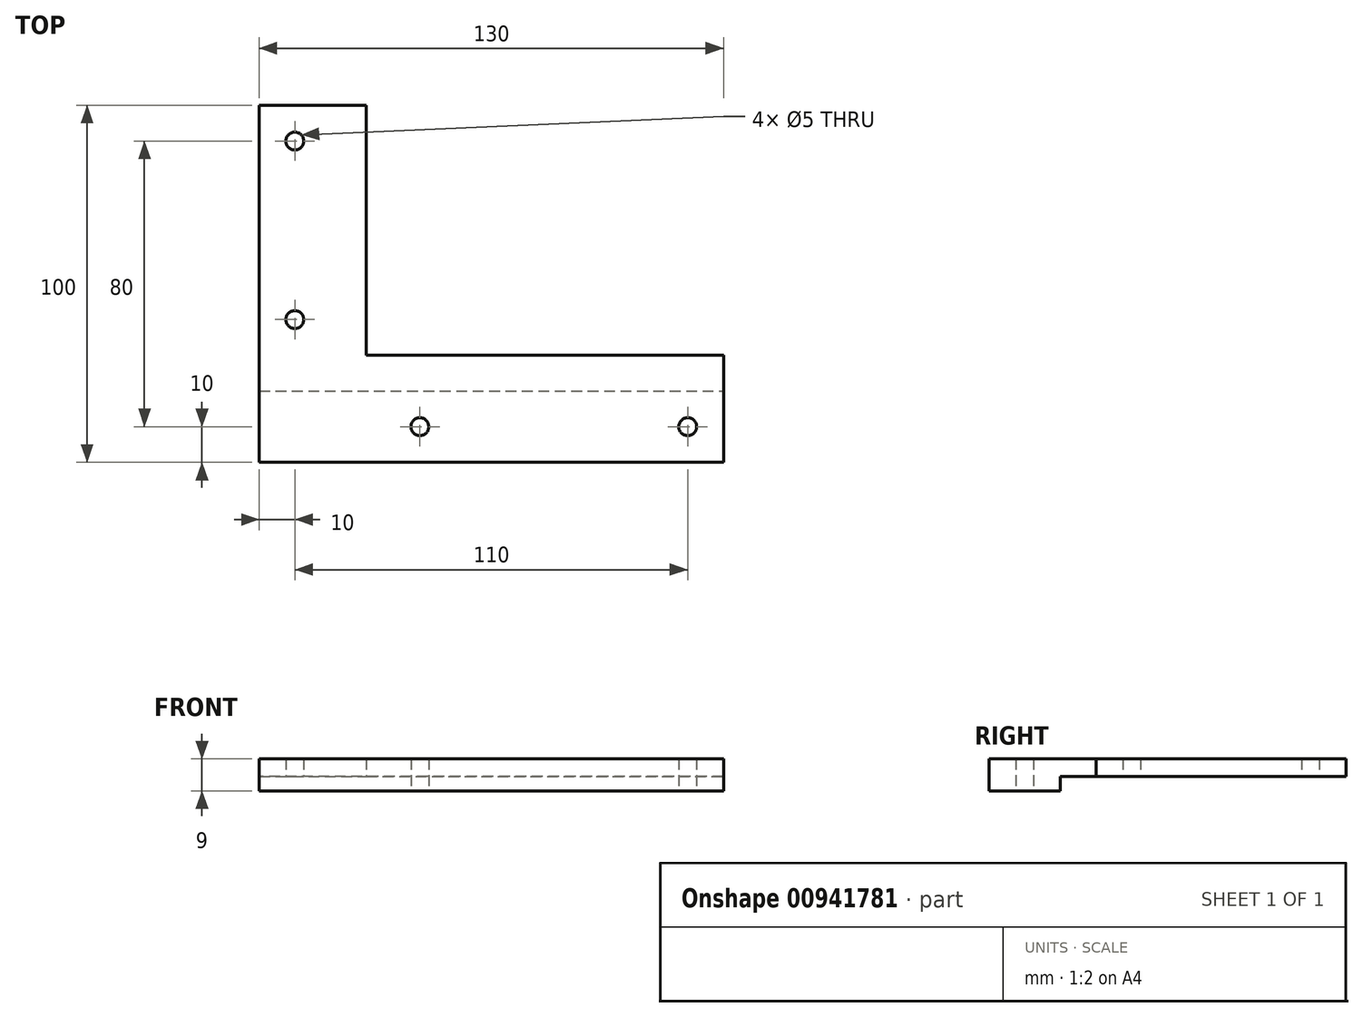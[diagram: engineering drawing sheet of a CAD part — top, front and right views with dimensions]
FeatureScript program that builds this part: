
annotation { "Feature Type Name" : "Feature", "Feature Type Description" : "" }
export const myFeature = defineFeature(function(context is Context, id is Id, definition is map)
    precondition{}
    {
        {
            var Q0;
            Q0=qCreatedBy(makeId("Top.planeOp"),FACE);
            var sketch = newSketch(context, id + "F0", { "sketchPlane" : qUnion([Q0])});
            skEllipticalArc(sketch, "E0", {});
            skLineSegment(sketch, "E1", {"start": v(-116.5, 0) * mm, "end": v(-116.5, -86.5) * mm});
            skPoint(sketch, "E1.endSnap0", {"position": v(0, -86.5) * mm});
            skLineSegment(sketch, "E2", {"start": v(-116.5, -86.5) * mm, "end": v(0, -86.5) * mm});
            skLineSegment(sketch, "E3", {"start": v(-116.5, 0) * mm, "end": v(-130, 0) * mm});
            skLineSegment(sketch, "E4", {"start": v(-130, 0) * mm, "end": v(-130, -100) * mm});
            skLineSegment(sketch, "E5", {"start": v(-130, -100) * mm, "end": v(0, -100) * mm});
            skLineSegment(sketch, "E6", {"start": v(0, -100) * mm, "end": v(0, -86.5) * mm});
            const initialGuessF0  = {"E0": [0, 0, 1, 0, 0.1165, 0.0865, 3.141592653589793, 4.71238898038469]};
            skSetInitialGuess(sketch, initialGuessF0);
            skSolve(sketch);
        }
        {
            var Q0;
            Q0=qSketchRegion(id+"F0",true);
            extrude(context, id + "F1", {"entities" : qUnion([Q0]), "depth" : 12 * mm, "offsetDistance" : 25 * mm});
        }
        {
            var Q0;
            Q0=makeQuery(id+"F1.opExtrude","SWEPT_FACE",FACE,{"disambiguationData":[OSD([sQuery(id+"F0.wireOp",EDGE,"E5")])]});
            var sketch = newSketch(context, id + "F2", { "sketchPlane" : qUnion([Q0])});
            skLineSegment(sketch, "E7.bottom", {"start": v(-130, 16) * mm, "end": v(0, 16) * mm});
            skLineSegment(sketch, "E7.top", {"start": v(-130, -4) * mm, "end": v(0, -4) * mm});
            skLineSegment(sketch, "E7.left", {"start": v(-130, 16) * mm, "end": v(-130, -4) * mm});
            skLineSegment(sketch, "E7.right", {"start": v(0, 16) * mm, "end": v(0, -4) * mm});
            skSolve(sketch);
        }
        {
            var Q0;
            Q0=qSketchRegion(id+"F2",true);
            extrude(context, id + "F3", {"entities" : qUnion([Q0]), "operationType" : NewBodyOperationType.ADD, "depth" : 5 * mm, "offsetDistance" : 25 * mm});
        }
        {
            var Q0;
            Q0=makeQuery(id+"F3.boolean.opBoolean","MERGE",FACE,{"derivedFrom":[makeQuery(id+"F1.opExtrude","SWEPT_FACE",FACE,{"disambiguationData":[OSD([sQuery(id+"F0.wireOp",EDGE,"E4")])]}),makeQuery(id+"F3.opExtrude","SWEPT_FACE",FACE,{"disambiguationData":[OSD([sQuery(id+"F2.wireOp",EDGE,"E7.left")])]})]});
            var sketch = newSketch(context, id + "F4", { "sketchPlane" : qUnion([Q0])});
            skLineSegment(sketch, "E8.bottom", {"start": v(105, 16) * mm, "end": v(0, 16) * mm});
            skLineSegment(sketch, "E8.top", {"start": v(105, -4) * mm, "end": v(0, -4) * mm});
            skLineSegment(sketch, "E8.left", {"start": v(105, 16) * mm, "end": v(105, -4) * mm});
            skLineSegment(sketch, "E8.right", {"start": v(0, 16) * mm, "end": v(0, -4) * mm});
            skSolve(sketch);
        }
        {
            var Q0;
            Q0=qSketchRegion(id+"F4",true);
            extrude(context, id + "F5", {"entities" : qUnion([Q0]), "operationType" : NewBodyOperationType.ADD, "depth" : 5 * mm, "offsetDistance" : 25 * mm});
        }
        {
            var Q0;
            Q0=makeQuery(id+"F5.boolean.opBoolean","MERGE",FACE,{"derivedFrom":[makeQuery(id+"F3.opExtrude","SWEPT_FACE",FACE,{"disambiguationData":[OSD([sQuery(id+"F2.wireOp",EDGE,"E7.bottom")])]}),makeQuery(id+"F5.opExtrude","SWEPT_FACE",FACE,{"disambiguationData":[OSD([sQuery(id+"F4.wireOp",EDGE,"E8.bottom")])]})]});
            var sketch = newSketch(context, id + "F6", { "sketchPlane" : qUnion([Q0])});
            skLineSegment(sketch, "E9", {"start": v(-135, 0) * mm, "end": v(-120, 0) * mm});
            skLineSegment(sketch, "E10", {"start": v(-120, 0) * mm, "end": v(-120, -90) * mm});
            skLineSegment(sketch, "E11", {"start": v(-120, -90) * mm, "end": v(0, -90) * mm});
            skLineSegment(sketch, "E12", {"start": v(0, -90) * mm, "end": v(0, -105) * mm});
            skLineSegment(sketch, "E13", {"start": v(0, -105) * mm, "end": v(-135, -105) * mm});
            skLineSegment(sketch, "E14", {"start": v(-135, -105) * mm, "end": v(-135, 0) * mm});
            skSolve(sketch);
        }
        {
            var Q0;
            Q0=makeQuery(id+"F5.boolean.opBoolean","MERGE",FACE,{"derivedFrom":[makeQuery(id+"F3.opExtrude","SWEPT_FACE",FACE,{"disambiguationData":[OSD([sQuery(id+"F2.wireOp",EDGE,"E7.top")])]}),makeQuery(id+"F5.opExtrude","SWEPT_FACE",FACE,{"disambiguationData":[OSD([sQuery(id+"F4.wireOp",EDGE,"E8.top")])]})]});
            var sketch = newSketch(context, id + "F7", { "sketchPlane" : qUnion([Q0])});
            skLineSegment(sketch, "E15.bottom", {"start": v(-130, 0) * mm, "end": v(-150, 0) * mm});
            skLineSegment(sketch, "E15.top", {"start": v(-130, 120) * mm, "end": v(-150, 120) * mm});
            skLineSegment(sketch, "E15.left", {"start": v(-130, 0) * mm, "end": v(-130, 120) * mm});
            skLineSegment(sketch, "E15.right", {"start": v(-150, 0) * mm, "end": v(-150, 120) * mm});
            skLineSegment(sketch, "E16.bottom", {"start": v(0, 100) * mm, "end": v(-150, 100) * mm});
            skLineSegment(sketch, "E16.top", {"start": v(0, 120) * mm, "end": v(-150, 120) * mm});
            skLineSegment(sketch, "E16.left", {"start": v(0, 100) * mm, "end": v(0, 120) * mm});
            skLineSegment(sketch, "E16.right", {"start": v(-150, 100) * mm, "end": v(-150, 120) * mm});
            skCircle(sketch, "E17", {"center": v(-140, 30) * mm, "radius": 2.5 * mm});
            skCircle(sketch, "E18", {"center": v(-140, 80) * mm, "radius": 2.5 * mm});
            skCircle(sketch, "E19", {"center": v(-105, 110) * mm, "radius": 2.5 * mm});
            skCircle(sketch, "E20", {"center": v(-30, 110) * mm, "radius": 2.5 * mm});
            skSolve(sketch);
        }
        {
            var Q0;
            Q0=qSketchRegion(id+"F7",true);
            extrude(context, id + "F8", {"entities" : qUnion([Q0]), "operationType" : NewBodyOperationType.ADD, "oppositeDirection" : true, "depth" : 25 * mm, "offsetDistance" : 25 * mm});
        }
        {
            var Q0;
            Q0=qSketchRegion(id+"F6",true);
            extrude(context, id + "F9", {"entities" : qUnion([Q0]), "operationType" : NewBodyOperationType.ADD, "depth" : 5 * mm, "offsetDistance" : 25 * mm});
        }
        {
            var Q0;
            Q0=qCreatedBy(makeId("Top.planeOp"),FACE);
            var sketch = newSketch(context, id + "F10", { "sketchPlane" : qUnion([Q0])});
            skLineSegment(sketch, "E21.bottom", {"start": v(-150, 0) * mm, "end": v(0, 0) * mm});
            skLineSegment(sketch, "E21.top", {"start": v(-150, -20) * mm, "end": v(0, -20) * mm});
            skLineSegment(sketch, "E21.left", {"start": v(-150, 0) * mm, "end": v(-150, -20) * mm});
            skLineSegment(sketch, "E21.right", {"start": v(0, 0) * mm, "end": v(0, -20) * mm});
            skLineSegment(sketch, "E22.bottom", {"start": v(0, -120) * mm, "end": v(-20, -120) * mm});
            skLineSegment(sketch, "E22.top", {"start": v(0, 0) * mm, "end": v(-20, 0) * mm});
            skLineSegment(sketch, "E22.left", {"start": v(0, -120) * mm, "end": v(0, 0) * mm});
            skLineSegment(sketch, "E22.right", {"start": v(-20, -120) * mm, "end": v(-20, 0) * mm});
            skSolve(sketch);
        }
        {
            var Q0;
            Q0=qSketchRegion(id+"F10",true);
            extrude(context, id + "F11", {"entities" : qUnion([Q0]), "operationType" : NewBodyOperationType.REMOVE, "endBound" : BoundingType.SYMMETRIC, "oppositeDirection" : true, "depth" : 50 * mm, "offsetDistance" : 25 * mm});
        }
        {
            var Q0;
            Q0=makeQuery(id+"F11.boolean.opBoolean","COPY",FACE,{"derivedFrom":makeQuery(id+"F11.opExtrude","SWEPT_FACE",FACE,{"disambiguationData":[OSD([sQuery(id+"F10.wireOp",EDGE,"E22.right")])]})});
            var sketch = newSketch(context, id + "F12", { "sketchPlane" : qUnion([Q0])});
            skPoint(sketch, "E23.oppositeSnap0", {"position": v(-92.6, 12) * mm});
            skLineSegment(sketch, "E23.bottom", {"start": v(-120, -4) * mm, "end": v(-20, -4) * mm});
            skLineSegment(sketch, "E23.top", {"start": v(-120, 12) * mm, "end": v(-20, 12) * mm});
            skLineSegment(sketch, "E23.left", {"start": v(-120, -4) * mm, "end": v(-120, 12) * mm});
            skLineSegment(sketch, "E23.right", {"start": v(-20, -4) * mm, "end": v(-20, 12) * mm});
            skSolve(sketch);
        }
        {
            var Q0;
            Q0=qSketchRegion(id+"F12",true);
            extrude(context, id + "F13", {"entities" : qUnion([Q0]), "operationType" : NewBodyOperationType.REMOVE, "oppositeDirection" : true, "depth" : 150 * mm, "offsetDistance" : 25 * mm});
        }
        {
            var Q0;
            Q0=makeQuery(id+"F9.opExtrude","SWEPT_FACE",FACE,{"disambiguationData":[OSD([sQuery(id+"F6.wireOp",EDGE,"E10")])]});
            var sketch = newSketch(context, id + "F14", { "sketchPlane" : qUnion([Q0])});
            skLineSegment(sketch, "E24.bottom", {"start": v(-100, 16) * mm, "end": v(-20, 16) * mm});
            skLineSegment(sketch, "E24.top", {"start": v(-100, 12) * mm, "end": v(-20, 12) * mm});
            skLineSegment(sketch, "E24.left", {"start": v(-100, 16) * mm, "end": v(-100, 12) * mm});
            skLineSegment(sketch, "E24.right", {"start": v(-20, 16) * mm, "end": v(-20, 12) * mm});
            skSolve(sketch);
        }
        {
            var Q0;
            Q0 = qSketchRegion(id + "F14", true);
            extrude(context, id + "F15", {"entities" : qUnion([Q0]), "operationType" : NewBodyOperationType.REMOVE, "endBound" : BoundingType.THROUGH_ALL, "oppositeDirection" : true, "depth" : 25 * mm, "offsetDistance" : 25 * mm});
        }
    });
